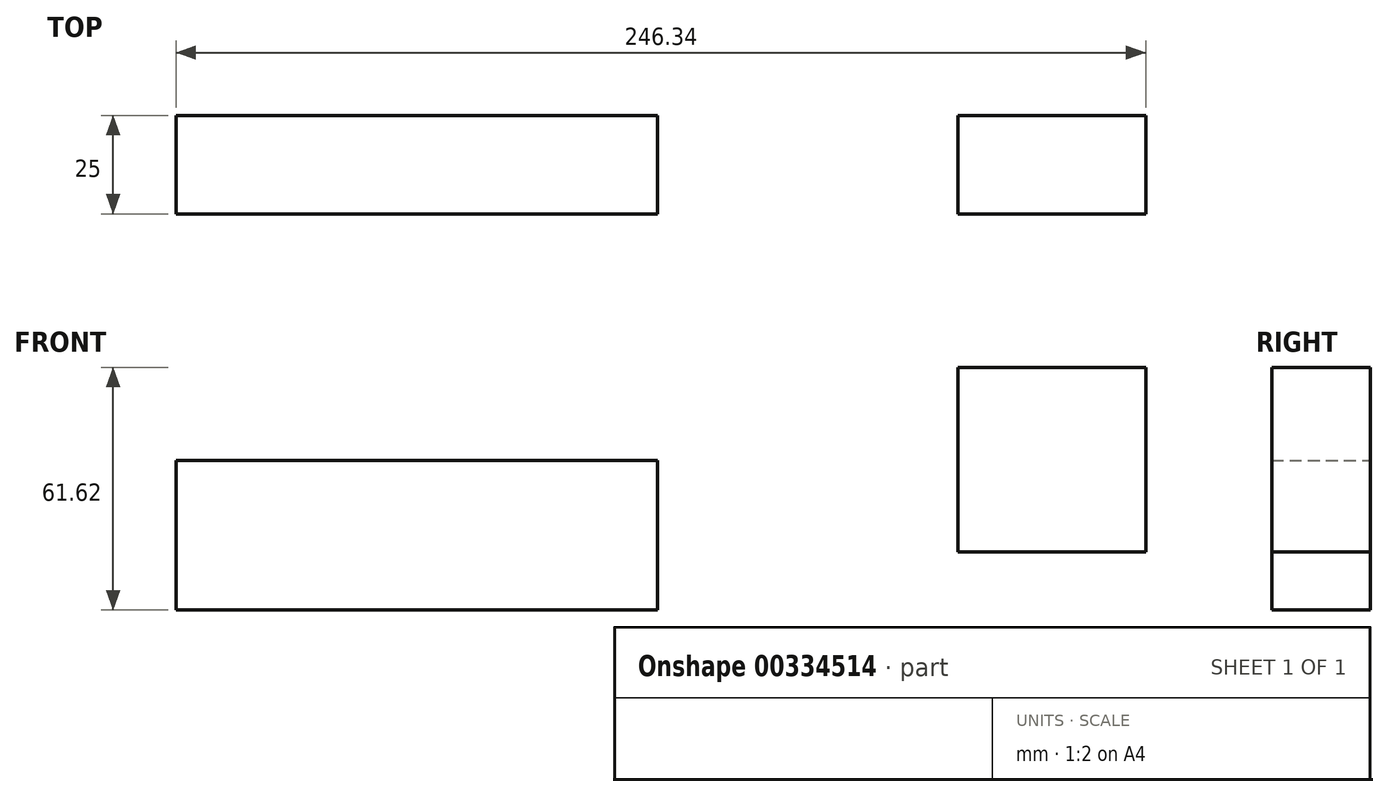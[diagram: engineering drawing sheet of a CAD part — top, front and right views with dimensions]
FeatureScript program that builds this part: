
annotation { "Feature Type Name" : "Feature", "Feature Type Description" : "" }
export const myFeature = defineFeature(function(context is Context, id is Id, definition is map)
    precondition{}
    {
        {
            var Q0;
            Q0=qCreatedBy(makeId("Front.planeOp"),FACE);
            var sketch = newSketch(context, id + "F0", { "sketchPlane" : qUnion([Q0])});
            skLineSegment(sketch, "E0.bottom", {"start": v(-94.93, 27.12) * mm, "end": v(27.43, 27.12) * mm});
            skLineSegment(sketch, "E0.top", {"start": v(-94.93, -10.9) * mm, "end": v(27.43, -10.9) * mm});
            skLineSegment(sketch, "E0.left", {"start": v(-94.93, 27.12) * mm, "end": v(-94.93, -10.9) * mm});
            skLineSegment(sketch, "E0.right", {"start": v(27.43, 27.12) * mm, "end": v(27.43, -10.9) * mm});
            skLineSegment(sketch, "E1.bottom", {"start": v(103.7, 50.7) * mm, "end": v(151.4, 50.7) * mm});
            skLineSegment(sketch, "E1.top", {"start": v(103.7, 3.79) * mm, "end": v(151.4, 3.79) * mm});
            skLineSegment(sketch, "E1.left", {"start": v(103.7, 50.7) * mm, "end": v(103.7, 3.79) * mm});
            skLineSegment(sketch, "E1.right", {"start": v(151.4, 50.7) * mm, "end": v(151.4, 3.79) * mm});
            skSolve(sketch);
        }
        {
            var Q0;
            Q0 = qSketchRegion(id + "F0", true);
            extrude(context, id + "F1", {"entities" : qUnion([Q0]), "depth" : 25 * mm});
        }
    });
